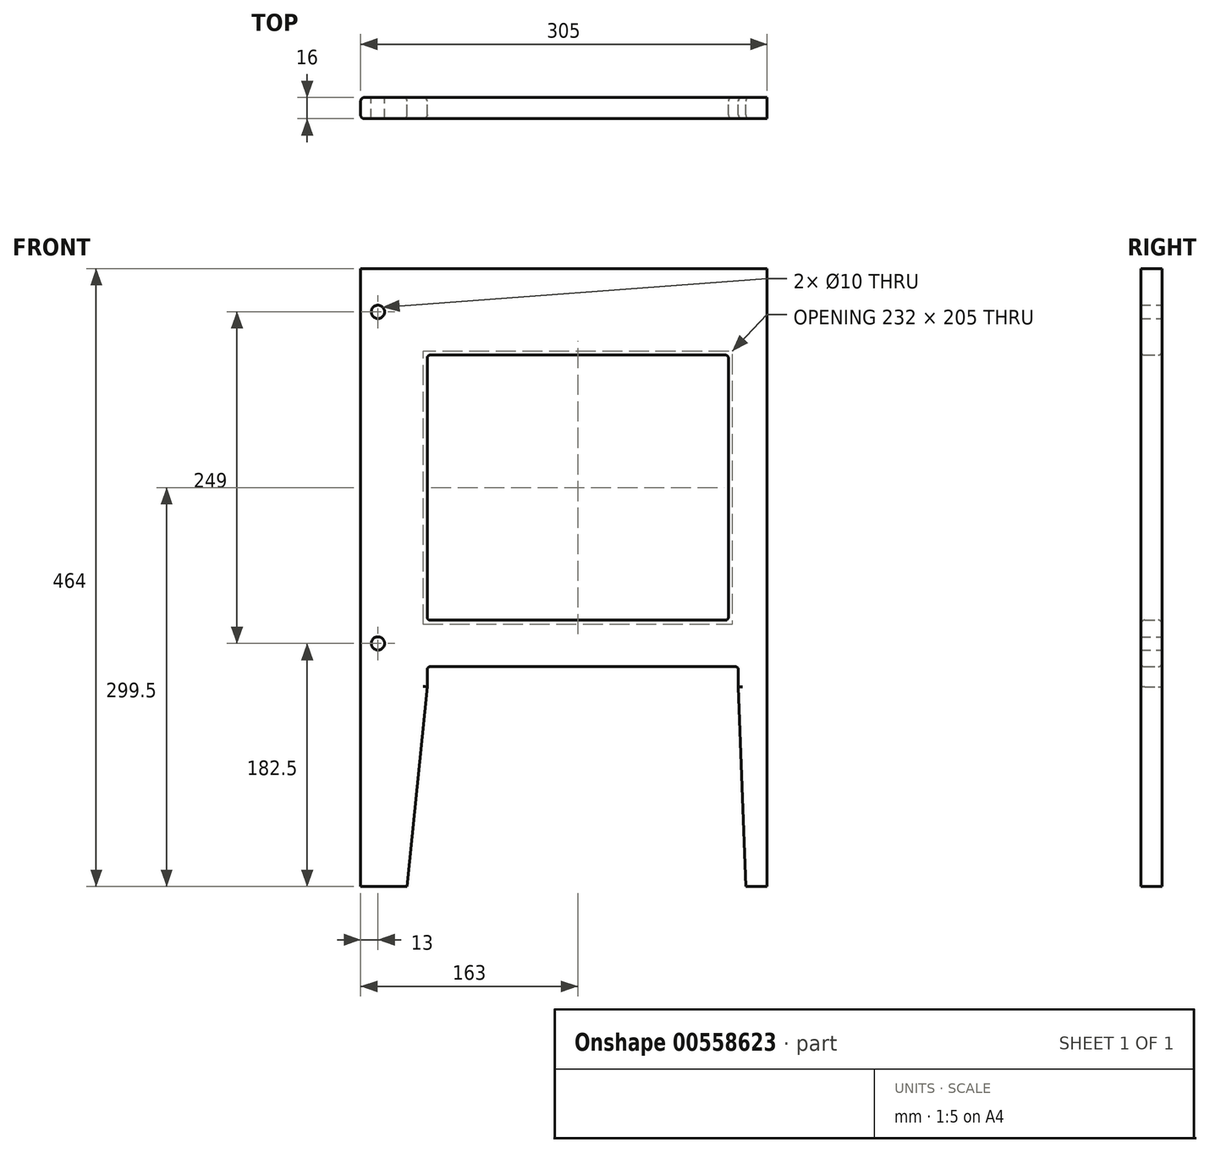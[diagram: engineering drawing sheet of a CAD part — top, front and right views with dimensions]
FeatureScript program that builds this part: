
annotation { "Feature Type Name" : "Feature", "Feature Type Description" : "" }
export const myFeature = defineFeature(function(context is Context, id is Id, definition is map)
    precondition{}
    {
        {
            var Q0;
            Q0=qCreatedBy(makeId("Front.planeOp"),FACE);
            var sketch = newSketch(context, id + "F0", { "sketchPlane" : qUnion([Q0])});
            skLineSegment(sketch, "E0.bottom", {"start": v(-152.5, -232) * mm, "end": v(-117.5, -232) * mm});
            skLineSegment(sketch, "E0.top", {"start": v(-152.5, 232) * mm, "end": v(152.5, 232) * mm});
            skLineSegment(sketch, "E0.left", {"start": v(-152.5, -232) * mm, "end": v(-152.5, 232) * mm});
            skLineSegment(sketch, "E0.right", {"start": v(152.5, -232) * mm, "end": v(152.5, 232) * mm});
            skPoint(sketch, "E0.middle", {"position": v(0, 0) * mm});
            skLineSegment(sketch, "E1.bottom", {"start": v(-100.5, 167) * mm, "end": v(121.5, 167) * mm});
            skLineSegment(sketch, "E1.top", {"start": v(-100.5, -32) * mm, "end": v(121.5, -32) * mm});
            skLineSegment(sketch, "E1.left", {"start": v(-102.5, 165) * mm, "end": v(-102.5, -30) * mm});
            skLineSegment(sketch, "E1.right", {"start": v(123.5, 165) * mm, "end": v(123.5, -30) * mm});
            skLineSegment(sketch, "E2", {"start": v(-117.5, -232) * mm, "end": v(-102.5, -82) * mm});
            skLineSegment(sketch, "E3", {"start": v(-102.5, -82) * mm, "end": v(-102.5, -69) * mm});
            skLineSegment(sketch, "E4", {"start": v(-100.5, -67) * mm, "end": v(129, -67) * mm});
            skLineSegment(sketch, "E5", {"start": v(131, -69) * mm, "end": v(131, -82) * mm});
            skLineSegment(sketch, "E6", {"start": v(131, -82) * mm, "end": v(136.5, -232) * mm});
            skPoint(sketch, "E7.visualSharp", {"position": v(-102.5, -32) * mm});
            skArc(sketch, "E7.filletArc", {"start": v(-102.5, -30) * mm, "mid": v(-101.91, -31.41) * mm, "end": v(-100.5, -32) * mm});
            skPoint(sketch, "E8.visualSharp", {"position": v(123.5, -32) * mm});
            skArc(sketch, "E8.filletArc", {"start": v(121.5, -32) * mm, "mid": v(122.91, -31.41) * mm, "end": v(123.5, -30) * mm});
            skPoint(sketch, "E9.visualSharp", {"position": v(123.5, 167) * mm});
            skArc(sketch, "E9.filletArc", {"start": v(123.5, 165) * mm, "mid": v(122.91, 166.41) * mm, "end": v(121.5, 167) * mm});
            skPoint(sketch, "E10.visualSharp", {"position": v(-102.5, 167) * mm});
            skArc(sketch, "E10.filletArc", {"start": v(-100.5, 167) * mm, "mid": v(-101.91, 166.41) * mm, "end": v(-102.5, 165) * mm});
            skPoint(sketch, "E11.visualSharp", {"position": v(-102.5, -67) * mm});
            skArc(sketch, "E11.filletArc", {"start": v(-100.5, -67) * mm, "mid": v(-101.91, -67.59) * mm, "end": v(-102.5, -69) * mm});
            skPoint(sketch, "E12.visualSharp", {"position": v(131, -67) * mm});
            skArc(sketch, "E12.filletArc", {"start": v(131, -69) * mm, "mid": v(130.41, -67.59) * mm, "end": v(129, -67) * mm});
            skLineSegment(sketch, "E13.trimOffspring", {"start": v(136.5, -232) * mm, "end": v(152.5, -232) * mm});
            skCircle(sketch, "E14", {"center": v(-139.5, 199.5) * mm, "radius": 5 * mm});
            skCircle(sketch, "E15", {"center": v(-139.5, -49.5) * mm, "radius": 5 * mm});
            skSolve(sketch);
        }
        {
            var Q0;
            Q0 = qSketchRegion(id + "F0", true);
            extrude(context, id + "F1", {"entities" : qUnion([Q0]), "depth" : 16 * mm, "offsetDistance" : 25 * mm});
        }
        {
            var Q0;
            Q0=makeQuery(id+"F1.opExtrude","CAP_EDGE",EDGE,{"disambiguationData":[OSD([sQuery(id+"F0.wireOp",EDGE,"E0.left")])],"isStart":false});
            var Q1;
            Q1=makeQuery(id+"F1.opExtrude","CAP_EDGE",EDGE,{"disambiguationData":[OSD([sQuery(id+"F0.wireOp",EDGE,"E0.left")])],"isStart":true});
            fillet(context, id + "F2", {"entities" : qUnion([Q0, Q1]), "radius" : 3 * mm, "tangentPropagation" : true, "allowEdgeOverflow" : false});
        }
        {
            var Q0;
            Q0=makeQuery(id+"F1.opExtrude","CAP_EDGE",EDGE,{"disambiguationData":[OSD([sQuery(id+"F0.wireOp",EDGE,"E1.bottom")])],"isStart":false});
            var Q1;
            Q1=makeQuery(id+"F1.opExtrude","CAP_EDGE",EDGE,{"disambiguationData":[OSD([sQuery(id+"F0.wireOp",EDGE,"E1.top")])],"isStart":true});
            fillet(context, id + "F3", {"entities" : qUnion([Q0, Q1]), "radius" : 3 * mm, "tangentPropagation" : true, "allowEdgeOverflow" : false});
        }
        {
            var Q0;
            Q0=makeQuery(id+"F1.opExtrude","CAP_EDGE",EDGE,{"disambiguationData":[OSD([sQuery(id+"F0.wireOp",EDGE,"E2")])],"isStart":false});
            var Q1;
            Q1=makeQuery(id+"F1.opExtrude","CAP_EDGE",EDGE,{"disambiguationData":[OSD([sQuery(id+"F0.wireOp",EDGE,"E3")])],"isStart":false});
            var Q2;
            Q2=makeQuery(id+"F1.opExtrude","CAP_EDGE",EDGE,{"disambiguationData":[OSD([sQuery(id+"F0.wireOp",EDGE,"E6")])],"isStart":false});
            var Q3;
            Q3=makeQuery(id+"F1.opExtrude","CAP_EDGE",EDGE,{"disambiguationData":[OSD([sQuery(id+"F0.wireOp",EDGE,"E2")])],"isStart":true});
            var Q4;
            Q4=makeQuery(id+"F1.opExtrude","CAP_EDGE",EDGE,{"disambiguationData":[OSD([sQuery(id+"F0.wireOp",EDGE,"E3")])],"isStart":true});
            var Q5;
            Q5=makeQuery(id+"F1.opExtrude","CAP_EDGE",EDGE,{"disambiguationData":[OSD([sQuery(id+"F0.wireOp",EDGE,"E4")])],"isStart":true});
            var Q6;
            Q6=makeQuery(id+"F1.opExtrude","CAP_EDGE",EDGE,{"disambiguationData":[OSD([sQuery(id+"F0.wireOp",EDGE,"E6")])],"isStart":true});
            fillet(context, id + "F4", {"entities" : qUnion([Q0, Q1, Q2, Q3, Q4, Q5, Q6]), "radius" : 3 * mm, "tangentPropagation" : true, "allowEdgeOverflow" : false});
        }
    });
